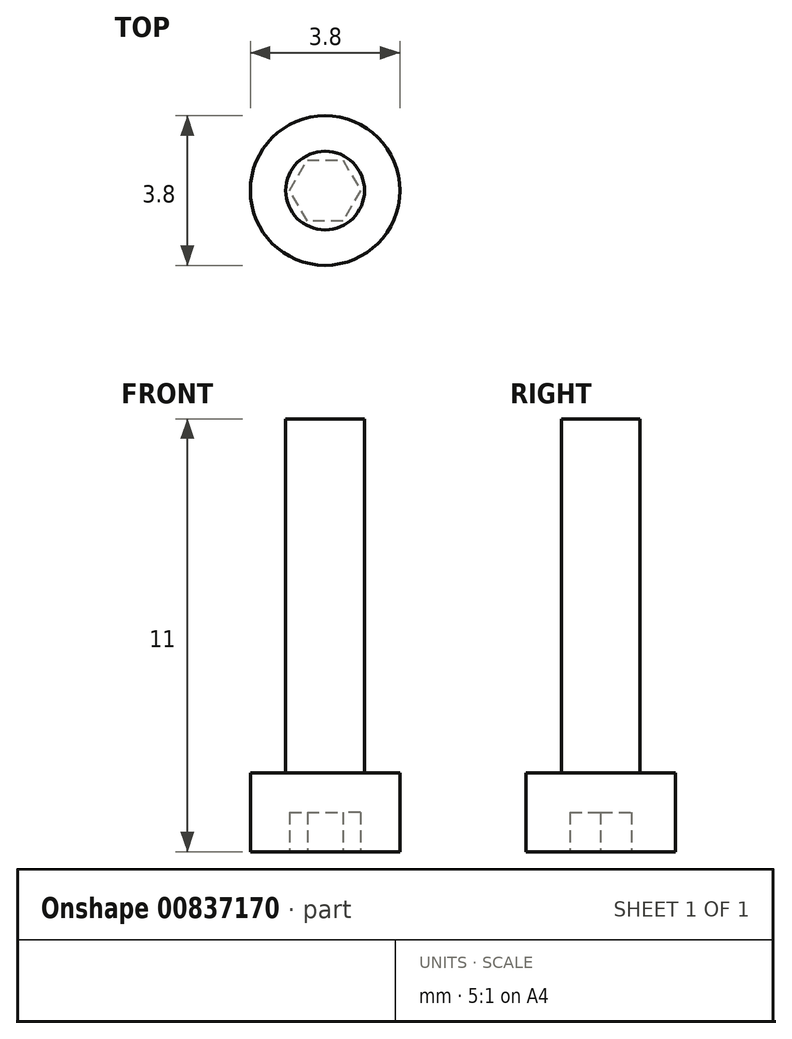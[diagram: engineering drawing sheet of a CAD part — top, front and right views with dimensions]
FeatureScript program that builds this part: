
annotation { "Feature Type Name" : "Feature", "Feature Type Description" : "" }
export const myFeature = defineFeature(function(context is Context, id is Id, definition is map)
    precondition{}
    {
        {
            var Q0;
            Q0=qCreatedBy(makeId("Top.planeOp"),FACE);
            var sketch = newSketch(context, id + "F0", { "sketchPlane" : qUnion([Q0])});
            skCircle(sketch, "E0", {"center": v(0, 0) * mm, "radius": 1.9 * mm});
            skCircle(sketch, "E1.cCircle", {"center": v(0, 0) * mm, "radius": 0.78 * mm, "construction": true});
            skLineSegment(sketch, "E1.0", {"start": v(-0.45, 0.78) * mm, "end": v(0.45, 0.78) * mm});
            skLineSegment(sketch, "E1.1", {"start": v(0.45, 0.78) * mm, "end": v(0.9, 0) * mm});
            skLineSegment(sketch, "E1.2", {"start": v(0.9, 0) * mm, "end": v(0.45, -0.78) * mm});
            skLineSegment(sketch, "E1.3", {"start": v(0.45, -0.78) * mm, "end": v(-0.45, -0.78) * mm});
            skLineSegment(sketch, "E1.4", {"start": v(-0.45, -0.78) * mm, "end": v(-0.9, 0) * mm});
            skLineSegment(sketch, "E1.5", {"start": v(-0.9, 0) * mm, "end": v(-0.45, 0.78) * mm});
            skPoint(sketch, "E1.0.midPoint", {"position": v(0, 0.78) * mm});
            skSolve(sketch);
        }
        {
            var Q0;
            Q0=makeQuery(id+"F0.imprint","IMPRINT",FACE,{"disambiguationData":[TD([[makeQuery(id+"F0.imprint","IMPRINT",EDGE,{"derivedFrom":sQuery(id+"F0.wireOp",EDGE,"E1.0")}),-1.0]])]});
            var Q1;
            Q1=makeQuery(id+"F0.imprint","IMPRINT",FACE,{"disambiguationData":[TD([[makeQuery(id+"F0.imprint","IMPRINT",EDGE,{"derivedFrom":sQuery(id+"F0.wireOp",EDGE,"E0")}),1.0]])]});
            extrude(context, id + "F1", {"entities" : qUnion([Q0, Q1]), "depth" : 2 * mm, "offsetDistance" : 25 * mm});
        }
        {
            var Q0;
            Q0=makeQuery(id+"F0.imprint","IMPRINT",FACE,{"disambiguationData":[TD([[makeQuery(id+"F0.imprint","IMPRINT",EDGE,{"derivedFrom":sQuery(id+"F0.wireOp",EDGE,"E1.0")}),-1.0]])]});
            extrude(context, id + "F2", {"entities" : qUnion([Q0]), "operationType" : NewBodyOperationType.REMOVE, "depth" : 1 * mm, "offsetDistance" : 25 * mm});
        }
        {
            var Q0;
            Q0=makeQuery(id+"F1.opExtrude","CAP_FACE",FACE,{"disambiguationData":[OSD([sQuery(id+"F0.wireOp",EDGE,"E0")])],"isStart":false});
            var sketch = newSketch(context, id + "F3", { "sketchPlane" : qUnion([Q0])});
            skCircle(sketch, "E2", {"center": v(0, 0) * mm, "radius": 1 * mm});
            skSolve(sketch);
        }
        {
            var Q0;
            Q0 = qSketchRegion(id + "F3", true);
            var Q1;
            Q1=makeQuery(id+"F3.imprint","IMPRINT",FACE,{"disambiguationData":[TD([[makeQuery(id+"F3.imprint","IMPRINT",EDGE,{"derivedFrom":sQuery(id+"F3.wireOp",EDGE,"E2")}),1.0]])]});
            extrude(context, id + "F4", {"entities" : qUnion([Q0, Q1]), "operationType" : NewBodyOperationType.ADD, "depth" : 9 * mm, "offsetDistance" : 25 * mm});
        }
    });
